annotation { "Feature Type Name" : "Feature", "Feature Type Description" : "" }
export const myFeature = defineFeature(function(context is Context, id is Id, definition is map)
    precondition{}
    {
        {
            var Q0;
            Q0=qCreatedBy(makeId("Front.planeOp"),FACE);
            var sketch = newSketch(context, id + "F0", { "sketchPlane" : qUnion([Q0])});
            skLineSegment(sketch, "E0.bottom", {"start": v(-76.2, 31.75) * mm, "end": v(76.2, 31.75) * mm});
            skLineSegment(sketch, "E0.top", {"start": v(-76.2, -31.75) * mm, "end": v(76.2, -31.75) * mm});
            skLineSegment(sketch, "E0.left", {"start": v(-88.9, 19.05) * mm, "end": v(-88.9, -19.05) * mm});
            skLineSegment(sketch, "E0.right", {"start": v(88.9, 19.05) * mm, "end": v(88.9, -19.05) * mm});
            skArc(sketch, "E1", {"start": v(-88.9, 19.05) * mm, "mid": v(-79.92, 22.77) * mm, "end": v(-76.2, 31.75) * mm});
            skArc(sketch, "E2", {"start": v(76.2, 31.75) * mm, "mid": v(79.92, 22.77) * mm, "end": v(88.9, 19.05) * mm});
            skArc(sketch, "E3", {"start": v(88.9, -19.05) * mm, "mid": v(79.92, -22.77) * mm, "end": v(76.2, -31.75) * mm});
            skArc(sketch, "E4", {"start": v(-76.2, -31.75) * mm, "mid": v(-79.92, -22.77) * mm, "end": v(-88.9, -19.05) * mm});
            skSolve(sketch);
        }
        {
            var Q0;
            Q0 = qSketchRegion(id + "F0", true);
            extrude(context, id + "F1", {"entities" : qUnion([Q0]), "depth" : 3.17 * mm});
        }
        {
            var Q0;
            Q0=makeQuery(id+"F1.opExtrude","CAP_FACE",FACE,{"disambiguationData":[OSD([sQuery(id+"F0.wireOp",EDGE,"E0.bottom"),sQuery(id+"F0.wireOp",EDGE,"E0.top"),sQuery(id+"F0.wireOp",EDGE,"E0.left"),sQuery(id+"F0.wireOp",EDGE,"E0.right"),sQuery(id+"F0.wireOp",EDGE,"E1"),sQuery(id+"F0.wireOp",EDGE,"E2"),sQuery(id+"F0.wireOp",EDGE,"E3"),sQuery(id+"F0.wireOp",EDGE,"E4")])],"isStart":false});
            var sketch = newSketch(context, id + "F2", { "sketchPlane" : qUnion([Q0])});
            skLineSegment(sketch, "E5", {"start": v(-88.9, 3.12) * mm, "end": v(88.9, 3.12) * mm, "construction": true});
            skLineSegment(sketch, "E6", {"start": v(88.9, -19) * mm, "end": v(-88.9, -19) * mm, "construction": true});
            skText(sketch, "E7", { "text": "UNCLE MEAT", "fontName": "NotoSerif-Bold.ttf"});
            skText(sketch, "E8", { "text": "SMOKERS", "fontName": "NotoSerif-Regular.ttf"});
            skLineSegment(sketch, "E9", {"start": v(88.9, 19.05) * mm, "end": v(-88.9, 19.05) * mm, "construction": true});
            const initialGuessF2  = {"E7": [-0.0762, 0.00312, 1, 0, 0.01605], "E8": [-0.0508, -0.019, 1, 0, 0.01536]};
            skSetInitialGuess(sketch, initialGuessF2);
            skSolve(sketch);
        }
        {
            var Q0;
            Q0 = qSketchRegion(id + "F2", true);
            extrude(context, id + "F3", {"entities" : qUnion([Q0]), "operationType" : NewBodyOperationType.ADD, "depth" : 3.17 * mm});
        }
        {
            var Q0;
            {var subQ0=sQuery(id+"F0.wireOp",EDGE,"E4");var subQ1=sQuery(id+"F0.wireOp",EDGE,"E3");var subQ2=sQuery(id+"F0.wireOp",EDGE,"E2");var subQ3=sQuery(id+"F0.wireOp",EDGE,"E1");var subQ4=sQuery(id+"F0.wireOp",EDGE,"E0.top");var subQ5=sQuery(id+"F0.wireOp",EDGE,"E0.right");var subQ6=sQuery(id+"F0.wireOp",EDGE,"E0.bottom");var subQ7=sQuery(id+"F0.wireOp",EDGE,"E0.left");Q0=makeQuery(id+"F3.boolean.opBoolean","SPLIT",FACE,{"disambiguationData":[TD([makeQuery(id+"F1.opExtrude","SWEPT_FACE",FACE,{"disambiguationData":[OSD([subQ6])]})])],"derivedFrom":makeQuery(id+"F1.opExtrude","CAP_FACE",FACE,{"disambiguationData":[OSD([subQ6,subQ4,subQ7,subQ5,subQ3,subQ2,subQ1,subQ0])],"isStart":false})});}
            var sketch = newSketch(context, id + "F4", { "sketchPlane" : qUnion([Q0])});
            skCircle(sketch, "E10", {"center": v(-72.4, 27.94) * mm, "radius": 0.8 * mm});
            skCircle(sketch, "E11", {"center": v(72.4, 27.94) * mm, "radius": 0.8 * mm});
            skCircle(sketch, "E12", {"center": v(72.4, -27.94) * mm, "radius": 0.8 * mm});
            skCircle(sketch, "E13", {"center": v(-72.4, -27.94) * mm, "radius": 0.8 * mm});
            skSolve(sketch);
        }
        {
            var Q0;
            Q0 = qSketchRegion(id + "F4", true);
            extrude(context, id + "F5", {"entities" : qUnion([Q0]), "operationType" : NewBodyOperationType.REMOVE, "oppositeDirection" : true, "depth" : 50.8 * mm});
        }
    });